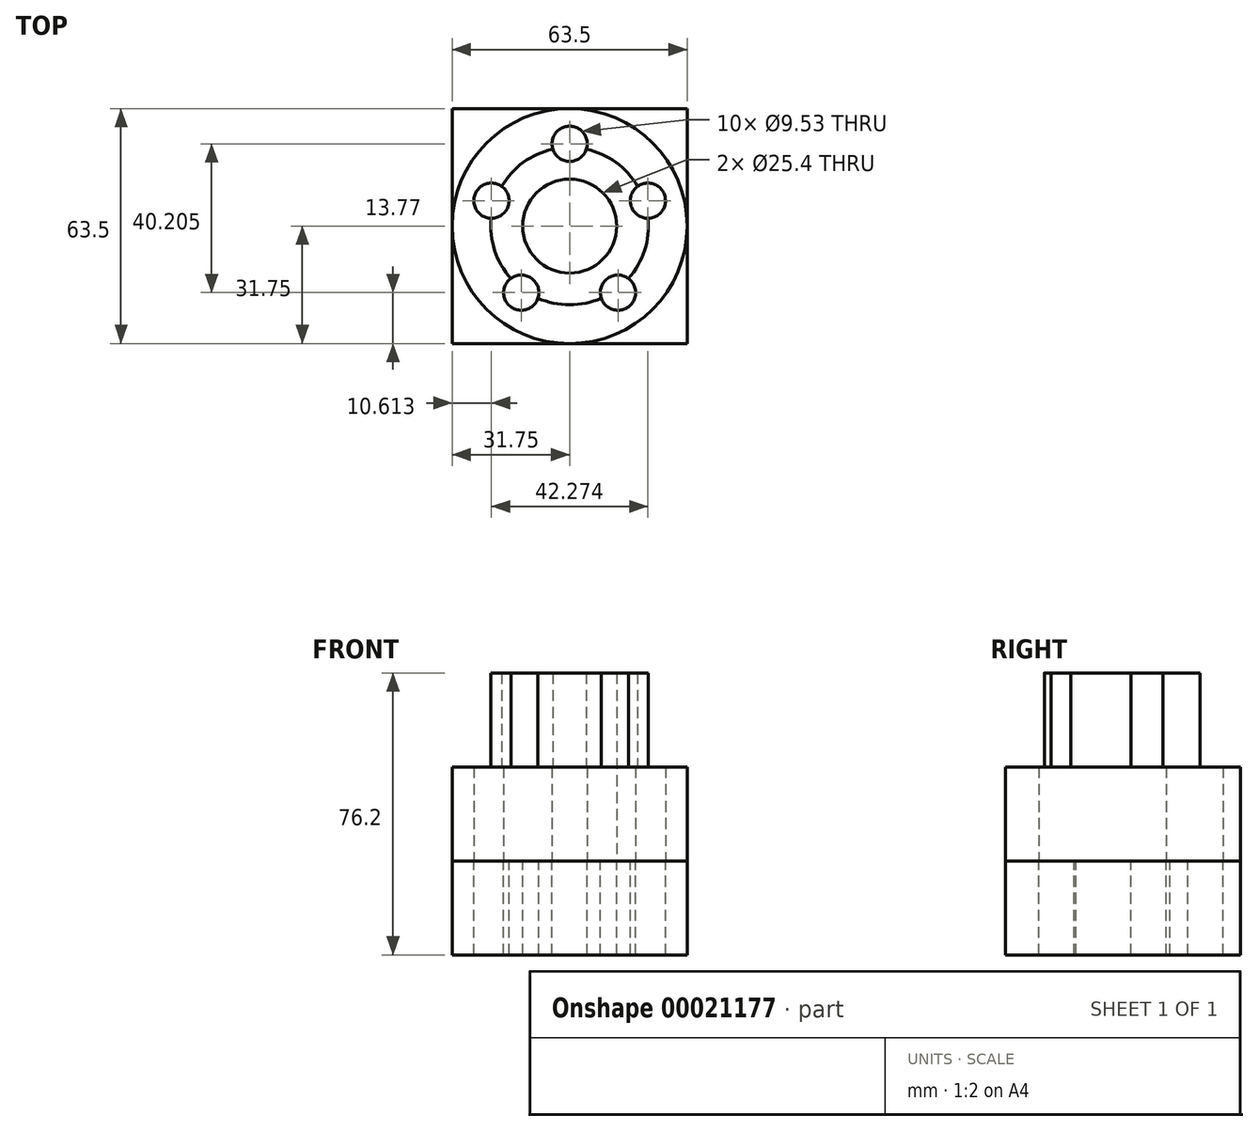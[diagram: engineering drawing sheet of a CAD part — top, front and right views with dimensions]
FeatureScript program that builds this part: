
annotation { "Feature Type Name" : "Feature", "Feature Type Description" : "" }
export const myFeature = defineFeature(function(context is Context, id is Id, definition is map)
    precondition{}
    {
        {
            var Q0;
            Q0=qCreatedBy(makeId("Top.planeOp"),FACE);
            var sketch = newSketch(context, id + "F0", { "sketchPlane" : qUnion([Q0])});
            skCircle(sketch, "E0", {"center": v(0, 0) * mm, "radius": 31.75 * mm});
            skCircle(sketch, "E1", {"center": v(0, 0) * mm, "radius": 12.7 * mm});
            skLineSegment(sketch, "E2", {"start": v(0, 12.7) * mm, "end": v(0, 31.75) * mm, "construction": true});
            skCircle(sketch, "E3", {"center": v(0, 22.23) * mm, "radius": 4.76 * mm});
            skCircle(sketch, "E4.1.0", {"center": v(-21.14, 6.87) * mm, "radius": 4.76 * mm});
            skCircle(sketch, "E4.2.0", {"center": v(-13.06, -17.98) * mm, "radius": 4.76 * mm});
            skCircle(sketch, "E4.3.0", {"center": v(13.06, -17.98) * mm, "radius": 4.76 * mm});
            skCircle(sketch, "E4.4.0", {"center": v(21.14, 6.87) * mm, "radius": 4.76 * mm});
            skLineSegment(sketch, "E5.rect.bottom", {"start": v(-31.75, 31.75) * mm, "end": v(31.75, 31.75) * mm});
            skLineSegment(sketch, "E5.rect.top", {"start": v(-31.75, -31.75) * mm, "end": v(31.75, -31.75) * mm});
            skLineSegment(sketch, "E5.rect.left", {"start": v(-31.75, 31.75) * mm, "end": v(-31.75, -31.75) * mm});
            skLineSegment(sketch, "E5.rect.right", {"start": v(31.75, 31.75) * mm, "end": v(31.75, -31.75) * mm});
            skSolve(sketch);
        }
        {
            var Q0;
            Q0=makeQuery(id+"F0.imprint","IMPRINT",FACE,{"disambiguationData":[TD([[makeQuery(id+"F0.imprint","IMPRINT",EDGE,{"derivedFrom":sQuery(id+"F0.wireOp",EDGE,"E1")}),-1.0]])]});
            extrude(context, id + "F1", {"entities" : qUnion([Q0]), "depth" : 25.4 * mm});
        }
        {
            var Q0;
            Q0=makeQuery(id+"F1.opExtrude","CAP_FACE",FACE,{"disambiguationData":[OSD([sQuery(id+"F0.wireOp",EDGE,"E0"),sQuery(id+"F0.wireOp",EDGE,"E1"),sQuery(id+"F0.wireOp",EDGE,"E3"),sQuery(id+"F0.wireOp",EDGE,"E4.1.0"),sQuery(id+"F0.wireOp",EDGE,"E4.2.0"),sQuery(id+"F0.wireOp",EDGE,"E4.3.0"),sQuery(id+"F0.wireOp",EDGE,"E4.4.0")])],"isStart":false});
            var sketch = newSketch(context, id + "F2", { "sketchPlane" : qUnion([Q0])});
            skCircle(sketch, "E6", {"center": v(0, 0) * mm, "radius": 21.28 * mm});
            skLineSegment(sketch, "E7", {"start": v(-4.76, 22.27) * mm, "end": v(4.76, 22.27) * mm, "construction": true});
            skSolve(sketch);
        }
        {
            var Q0;
            Q0=makeQuery(id+"F2.imprint","IMPRINT",FACE,{"disambiguationData":[TD([[makeQuery(id+"F2.imprint","IMPRINT",EDGE,{"derivedFrom":makeQuery(id+"F1.opExtrude","CAP_EDGE",EDGE,{"disambiguationData":[OSD([sQuery(id+"F0.wireOp",EDGE,"E1")])],"isStart":false})}),-1.0]])]});
            var Q1;
            Q1=sQuery(id+"F2.wireOp",EDGE,"E6");
            extrude(context, id + "F3", {"entities" : qUnion([Q0]), "operationType" : NewBodyOperationType.ADD, "surfaceEntities" : qUnion([Q1]), "depth" : 25.4 * mm});
        }
        {
            var Q0;
            Q0=makeQuery(id+"F0.imprint","IMPRINT",FACE,{"disambiguationData":[TD([[makeQuery(id+"F0.imprint","IMPRINT",EDGE,{"derivedFrom":sQuery(id+"F0.wireOp",EDGE,"E1")}),-1.0]])]});
            var Q1;
            {var subQ0=sQuery(id+"F0.wireOp",EDGE,"E5.rect.left");var subQ1=sQuery(id+"F0.wireOp",EDGE,"E0");var subQ2=makeQuery(id+"F0.imprint","INTERSECT",VERTEX,{"derivedFrom":[subQ1,subQ0]});Q1=makeQuery(id+"F0.imprint","IMPRINT",FACE,{"disambiguationData":[TD([[makeQuery(id+"F0.imprint","IMPRINT",EDGE,{"disambiguationData":[TD([[subQ2,-1.0]])],"derivedFrom":subQ1}),-1.0]])]});}
            var Q2;
            {var subQ1=sQuery(id+"F0.wireOp",EDGE,"E0");var subQ3=sQuery(id+"F0.wireOp",EDGE,"E5.rect.bottom");var subQ5=makeQuery(id+"F0.imprint","INTERSECT",VERTEX,{"derivedFrom":[subQ1,subQ3]});Q2=makeQuery(id+"F0.imprint","IMPRINT",FACE,{"disambiguationData":[TD([[makeQuery(id+"F0.imprint","IMPRINT",EDGE,{"disambiguationData":[TD([[subQ5,-1.0]])],"derivedFrom":subQ1}),-1.0]])]});}
            var Q3;
            {var subQ0=sQuery(id+"F0.wireOp",EDGE,"E5.rect.right");var subQ1=sQuery(id+"F0.wireOp",EDGE,"E0");var subQ2=makeQuery(id+"F0.imprint","INTERSECT",VERTEX,{"derivedFrom":[subQ1,subQ0]});Q3=makeQuery(id+"F0.imprint","IMPRINT",FACE,{"disambiguationData":[TD([[makeQuery(id+"F0.imprint","IMPRINT",EDGE,{"disambiguationData":[TD([[subQ2,1.0]])],"derivedFrom":subQ1}),-1.0]])]});}
            var Q4;
            {var subQ1=sQuery(id+"F0.wireOp",EDGE,"E0");var subQ3=sQuery(id+"F0.wireOp",EDGE,"E5.rect.bottom");var subQ5=makeQuery(id+"F0.imprint","INTERSECT",VERTEX,{"derivedFrom":[subQ1,subQ3]});Q4=makeQuery(id+"F0.imprint","IMPRINT",FACE,{"disambiguationData":[TD([[makeQuery(id+"F0.imprint","IMPRINT",EDGE,{"disambiguationData":[TD([[subQ5,1.0]])],"derivedFrom":subQ1}),-1.0]])]});}
            extrude(context, id + "F4", {"entities" : qUnion([Q0, Q1, Q2, Q3, Q4]), "oppositeDirection" : true, "depth" : 25.4 * mm});
        }
    });
